# Revit family: Faucet-Deck_Mount-Bath-KOHLER-Forte_Sculpted-K-T10292_1
name_source: partatom
category: Plumbing Fixtures
units: mm (PartAtom-declared; Revit-internal decimal feet)

## family parameters
Cut with Voids When Loaded = No
Host = Face
OmniClass Number = 23.31.11.00
OmniClass Title = Faucets
Part Type = Normal
Room Calculation Point = No
Round Connector Dimension = Use Diameter
Shared = No

## types (3) — shared parameters
ADA Compliant = Yes
Assembly Code = D2010
CW Connection = Yes
Cold Water Inlet = Cold Water Inlet
Date Modified = 11/17/2022
Default Elevation = 36"
Description = Deck-mount bath faucet trim for high-flow valve with diverter spout, valve not included
Drain Included = No
Flow Rate = 0 GPM
HW Connection = Yes
Handle Clearance = 2 7/8"
Height = 6 3/4"
Hot Water Inlet = Hot Water Inlet
Length = 7 1/4"
Manufacturer = Kohler Co.
Master Format 2014 = 22 41 39
Master Format 2014 Name = Residential Faucets, Supplies, and Trim
Material = Premium Metal Construction
Pressure = 0.00 psi
Product Documentation Link = https://www.us.kohler.com
Product Name = Forte Sculpted
Product Page URL = http://www.us.kohler.com
Spout Reach = 7 1/4"
URL = https://www.us.kohler.com
Vent Connection = No
Waste Connection = No
Waste Water Outlet = Waste Water Outlet
WaterSense Certified = No

## per-type parameters (varying)
| type | Finish | Model | Type |
| BN-Vibrant Brushed Nickel | Kohler-Metal-BN-Vibrant_Brushed_Nickel | K-T10292-4-BN | 2 |
| CP-Polished Chrome | Kohler-Metal-CP-Polished_Chrome | K-T10292-4-CP | 3 |
| 0-White | Kohler-Metal-0-White | K-T10292-4-0 | 1 |

## geometry (parser evidence)
native form markers: Sweep x7
no freeform markers — native parametric forms only
